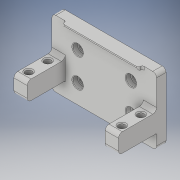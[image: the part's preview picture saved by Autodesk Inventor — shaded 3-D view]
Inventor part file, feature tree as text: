
AUTODESK INVENTOR PART (.ipt)
format: ipt  version: 2019 (Build 230136000, 136)  size: 222,208 bytes
history: native  units: mm
features: sketch x4, other x3
ambient origin geometry x8: Origin, YZ Plane, XZ Plane, XY Plane, X Axis, Y Axis, Z Axis, Center Point
bodies: Solid1 (feature_tree)
feature tree (7):
  other  "big_servo_hold_MIR.ipt"
  other  "Solid1::big_servo_hold_MIR.ipt"
  other  "TaggingFeature1"
  sketch  "Sketch1"  dims[d0=10.0mm]
  sketch  "Sketch2"
  sketch  "Sketch3"
  sketch  "Sketch4"
